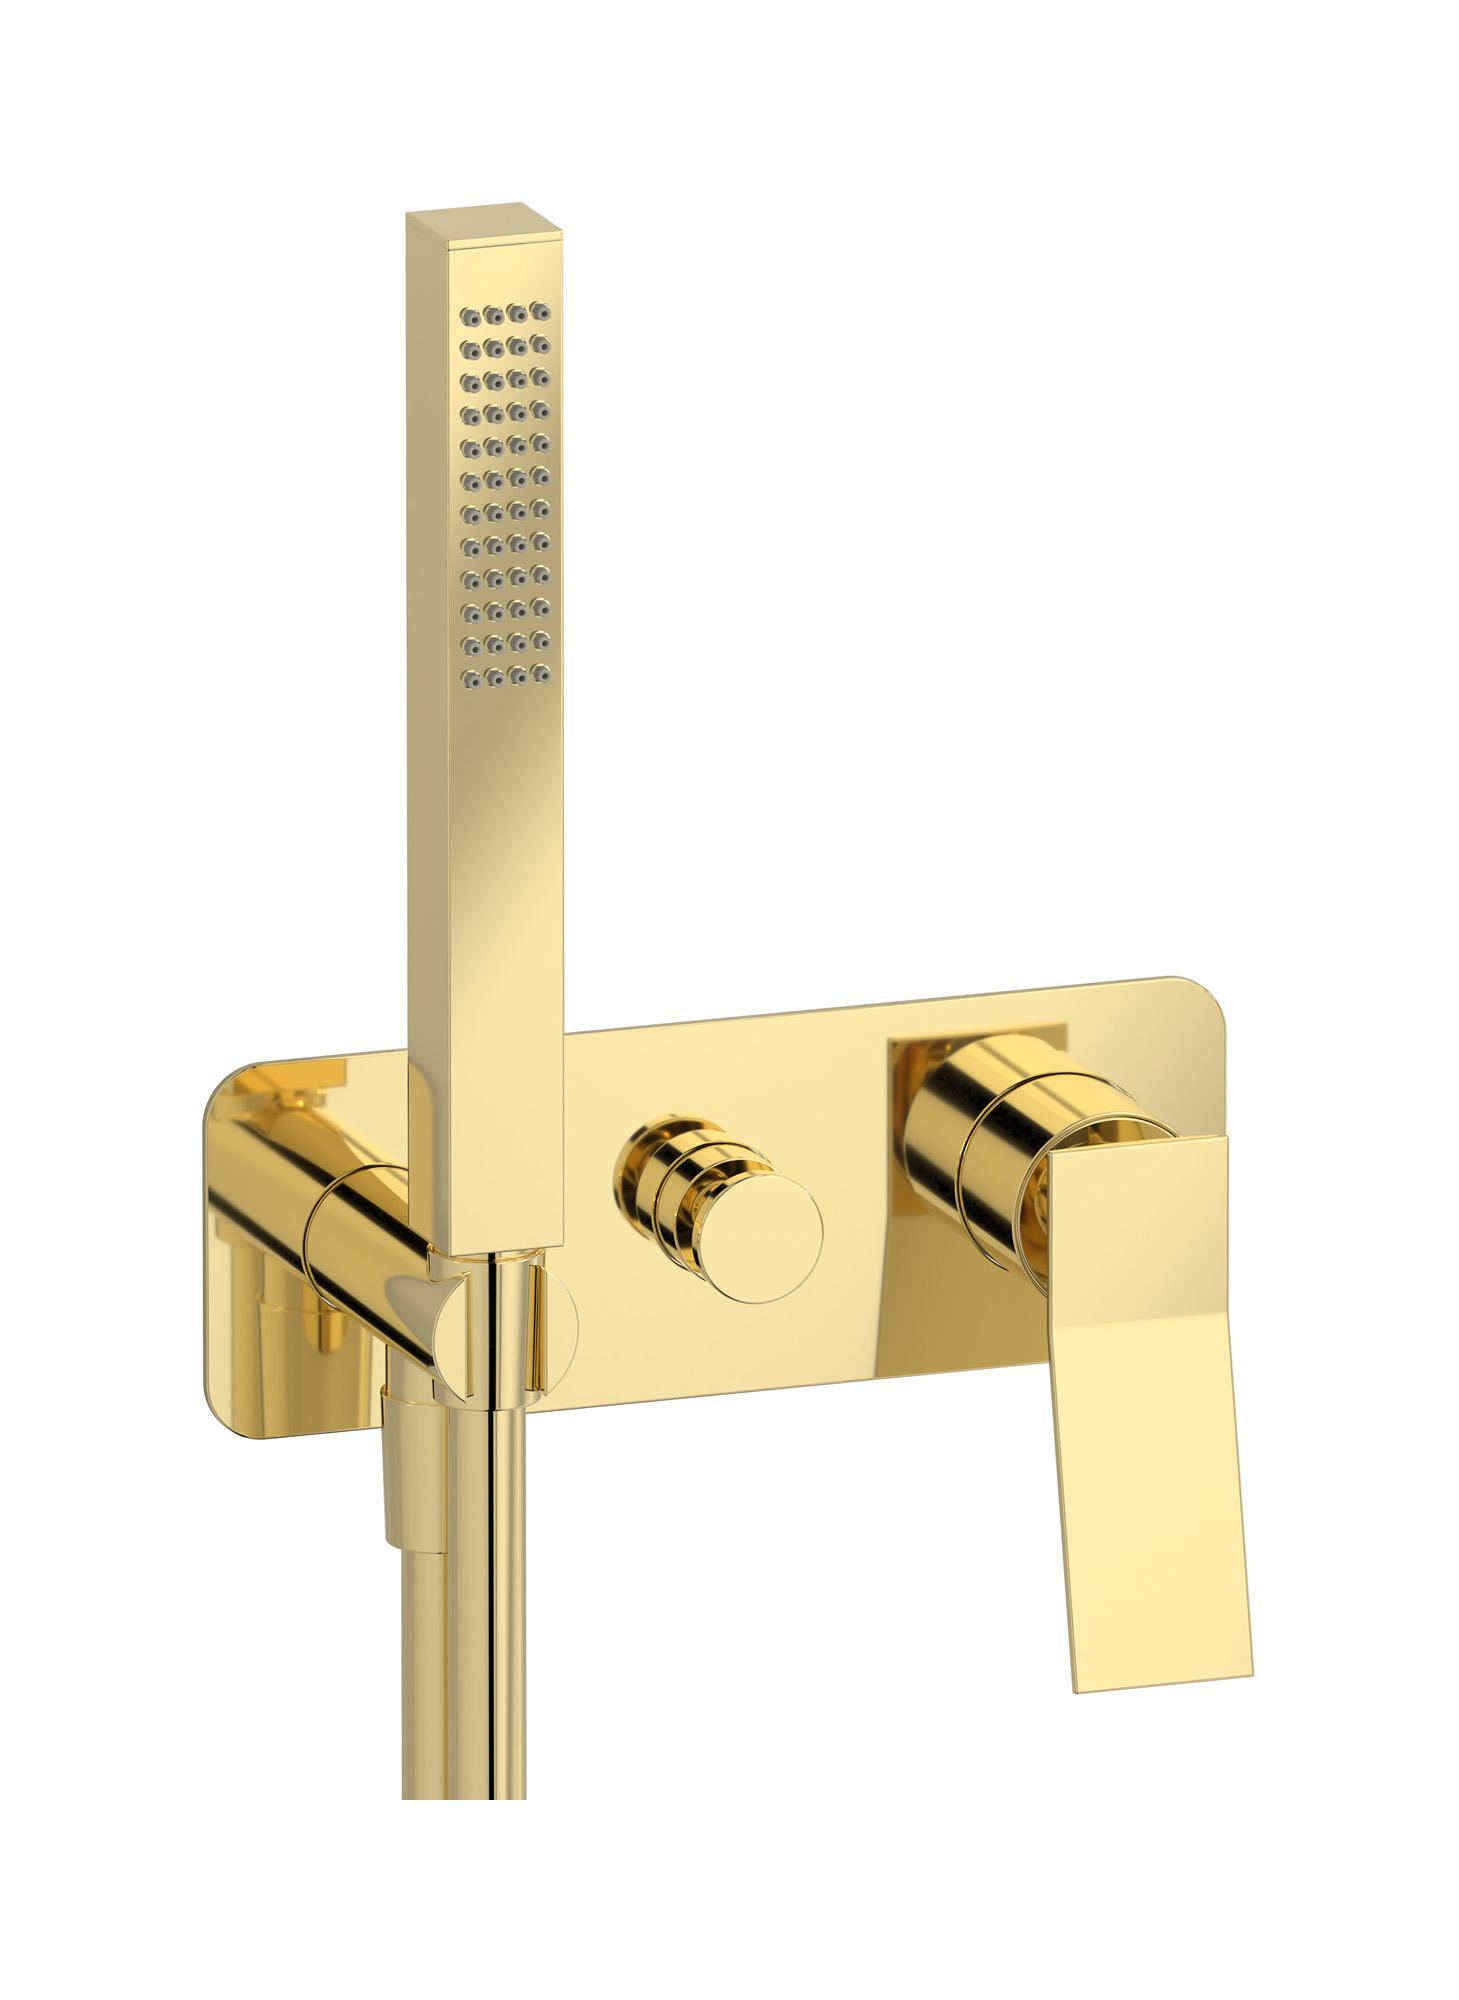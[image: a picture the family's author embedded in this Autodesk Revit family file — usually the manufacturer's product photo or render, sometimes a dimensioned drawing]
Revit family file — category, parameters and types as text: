
# Revit family: WA313
name_source: partatom
category: Apparecchi idraulici
units: mm (PartAtom-declared; Revit-internal decimal feet)

## family parameters
Basato su piano di lavoro = No
Condiviso = No
Mantieni orientamento annotazione = No
Numero OmniClass = 23.45.55.17
Punto di calcolo locali = No
Quota connettore circolare = Usa diametro
Sempre verticale = Sì
Taglio con vuoti quando caricato = No
Tipo di parte = Normale
Titolo OmniClass = Mixing Faucets

## types (12) — shared parameters
Cold water inlet = 10 mm  [stored 0.0328084 ft]
Commenti sul tipo = Wall mixer
Connessione CW = No
Connessione HW = No
Connessione di scarico = No
Connessione di ventilazione = No
Descrizione = Exposed parts for manual wall mixer with two ways diverter and shower kit
Hot water inlet = 10 mm  [stored 0.0328084 ft]
Produttore = IB Rubinetterie S.p.A.
URL = https://www.weareib.it
zero-valued in all types: Prospetto di default

## per-type parameters (varying)
| type | Finishes surface | Immagine tipo | Modello |
| Chrome | IB_Chrome | WA313CC.jpg | WA313CC |
| Brushed nickel | IB_Brushed nickel | WA313SS.jpg | WA313SS |
| Matt black | IB_matt black | WA313NP.jpg | WA313NP |
| Matt white | IB_matt white | WA313BO.jpg | WA313BO |
| Black chrome | IB_Black chrome | WA313CF.jpg | WA313CF |
| Brushed black chrome | IB_Brushed black chrome | WA313CS.jpg | WA313CS |
| Pale gold | IB_Pale gold | WA313II.jpg | WA313II |
| Brushed pale gold | IB_brushed pale gold | WA313IS.jpg | WA313IS |
| Rose gold | IB_Rose gold | WA313RS.jpg | WA313RS |
| Brushed rose gold | IB_Brushed rose gold | WA313SR.jpg | WA313SR |
| Gold | IB_gold | WA313OO.jpg | WA313OO |
| Brushed gold | IB_brushed gold | WA313OS.jpg | WA313OS |

note: [stored X ft] marks values corroborated as IEEE doubles in the binary element streams (Revit-internal decimal feet)
